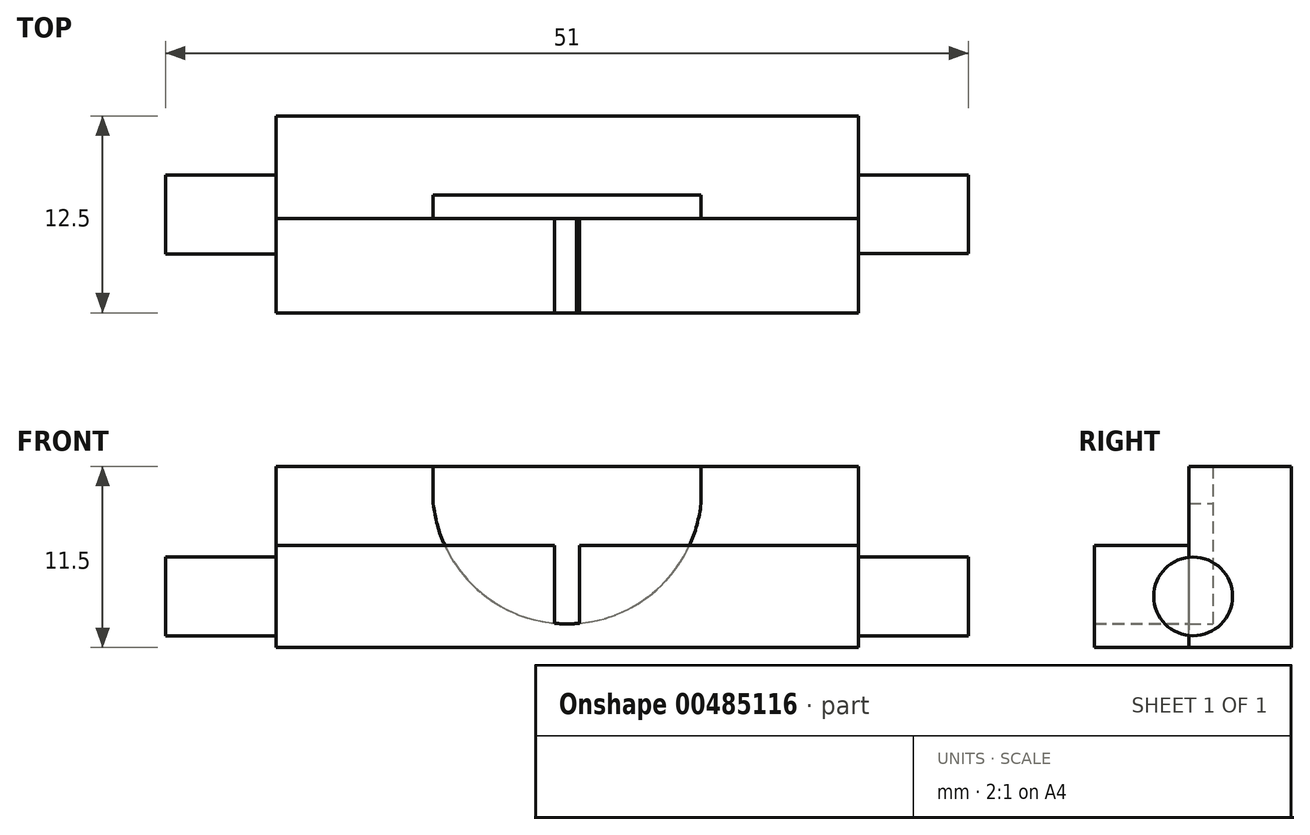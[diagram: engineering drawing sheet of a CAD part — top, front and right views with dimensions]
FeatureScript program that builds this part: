
annotation { "Feature Type Name" : "Feature", "Feature Type Description" : "" }
export const myFeature = defineFeature(function(context is Context, id is Id, definition is map)
    precondition{}
    {
        {
            var Q0;
            Q0=qCreatedBy(makeId("Front.planeOp"),FACE);
            var sketch = newSketch(context, id + "F0", { "sketchPlane" : qUnion([Q0])});
            skLineSegment(sketch, "E0.bottom", {"start": v(-8.5, 7.64) * mm, "end": v(8.5, 7.64) * mm, "construction": true});
            skLineSegment(sketch, "E0.top", {"start": v(-8.5, -7.64) * mm, "end": v(8.5, -7.64) * mm, "construction": true});
            skLineSegment(sketch, "E0.left", {"start": v(-8.5, 7.64) * mm, "end": v(-8.5, -7.64) * mm, "construction": true});
            skLineSegment(sketch, "E0.right", {"start": v(8.5, 7.64) * mm, "end": v(8.5, -7.64) * mm, "construction": true});
            skPoint(sketch, "E0.middle", {"position": v(0, 0) * mm});
            skLineSegment(sketch, "E1", {"start": v(0, 7.64) * mm, "end": v(0, -7.64) * mm, "construction": true});
            skLineSegment(sketch, "E2", {"start": v(-8.5, 0) * mm, "end": v(8.5, 0) * mm, "construction": true});
            skArc(sketch, "E3", {"start": v(-8.5, 0) * mm, "mid": v(0, -7.64) * mm, "end": v(8.5, 0) * mm});
            skLineSegment(sketch, "E4.bottom", {"start": v(-8.5, 7.64) * mm, "end": v(-20.5, 7.64) * mm, "construction": true});
            skLineSegment(sketch, "E4.top", {"start": v(-8.5, -7.64) * mm, "end": v(-20.5, -7.64) * mm, "construction": true});
            skLineSegment(sketch, "E4.right", {"start": v(-20.5, 7.64) * mm, "end": v(-20.5, -7.64) * mm, "construction": true});
            skLineSegment(sketch, "E5.bottom", {"start": v(8.5, 7.64) * mm, "end": v(20.5, 7.64) * mm, "construction": true});
            skLineSegment(sketch, "E5.top", {"start": v(8.5, -7.64) * mm, "end": v(20.5, -7.64) * mm, "construction": true});
            skLineSegment(sketch, "E5.right", {"start": v(20.5, 7.64) * mm, "end": v(20.5, -7.64) * mm, "construction": true});
            skLineSegment(sketch, "E6", {"start": v(-20.5, 2.36) * mm, "end": v(20.5, 2.36) * mm, "construction": true});
            skLineSegment(sketch, "E7", {"start": v(-18.5, 7.64) * mm, "end": v(-18.5, -7.64) * mm, "construction": true});
            skLineSegment(sketch, "E8", {"start": v(18.5, 7.64) * mm, "end": v(18.5, -7.64) * mm, "construction": true});
            skLineSegment(sketch, "E9.bottom", {"start": v(-20.5, -7.64) * mm, "end": v(20.5, -7.64) * mm, "construction": true});
            skLineSegment(sketch, "E9.top", {"start": v(-20.5, -9.14) * mm, "end": v(20.5, -9.14) * mm, "construction": true});
            skLineSegment(sketch, "E9.left", {"start": v(-20.5, -7.64) * mm, "end": v(-20.5, -9.14) * mm, "construction": true});
            skLineSegment(sketch, "E9.right", {"start": v(20.5, -7.64) * mm, "end": v(20.5, -9.14) * mm, "construction": true});
            skLineSegment(sketch, "E10", {"start": v(-18.5, 2.36) * mm, "end": v(-18.5, -9.14) * mm});
            skLineSegment(sketch, "E11", {"start": v(-18.5, -9.14) * mm, "end": v(18.5, -9.14) * mm});
            skLineSegment(sketch, "E12", {"start": v(18.5, -9.14) * mm, "end": v(18.5, 2.36) * mm});
            skLineSegment(sketch, "E13", {"start": v(18.5, 2.36) * mm, "end": v(8.5, 2.36) * mm});
            skLineSegment(sketch, "E14", {"start": v(8.5, 2.36) * mm, "end": v(8.5, 0) * mm});
            skLineSegment(sketch, "E15", {"start": v(-18.5, 2.36) * mm, "end": v(-8.5, 2.36) * mm});
            skLineSegment(sketch, "E16", {"start": v(-8.5, 2.36) * mm, "end": v(-8.5, 0) * mm});
            skLineSegment(sketch, "E17", {"start": v(-8.5, 2.36) * mm, "end": v(8.5, 2.36) * mm});
            skLineSegment(sketch, "E18", {"start": v(-20.5, 7.64) * mm, "end": v(-20.5, -7.64) * mm});
            skLineSegment(sketch, "E19", {"start": v(-20.5, -7.64) * mm, "end": v(-20.5, -9.14) * mm});
            skLineSegment(sketch, "E20", {"start": v(-18.5, -9.14) * mm, "end": v(-20.5, -9.14) * mm});
            skLineSegment(sketch, "E21", {"start": v(20.5, -9.14) * mm, "end": v(18.5, -9.14) * mm});
            skLineSegment(sketch, "E22", {"start": v(20.5, -9.14) * mm, "end": v(20.5, 2.36) * mm});
            skLineSegment(sketch, "E23", {"start": v(18.5, 2.36) * mm, "end": v(20.5, 2.36) * mm});
            skLineSegment(sketch, "E24", {"start": v(-18.5, 2.36) * mm, "end": v(-20.5, 2.36) * mm});
            skLineSegment(sketch, "E25", {"start": v(-20.5, 2.36) * mm, "end": v(-20.5, -9.14) * mm});
            skSolve(sketch);
        }
        {
            var Q0;
            Q0=makeQuery(id+"F0.imprint","IMPRINT",FACE,{"disambiguationData":[TD([[makeQuery(id+"F0.imprint","IMPRINT",EDGE,{"derivedFrom":sQuery(id+"F0.wireOp",EDGE,"E3")}),1.0]])]});
            extrude(context, id + "F1", {"entities" : qUnion([Q0]), "depth" : 5 * mm});
        }
        {
            var Q0;
            Q0=makeQuery(id+"F0.imprint","IMPRINT",FACE,{"disambiguationData":[TD([[makeQuery(id+"F0.imprint","IMPRINT",EDGE,{"derivedFrom":sQuery(id+"F0.wireOp",EDGE,"E3")}),-1.0]])]});
            extrude(context, id + "F2", {"entities" : qUnion([Q0]), "operationType" : NewBodyOperationType.ADD, "depth" : 6.5 * mm});
        }
        {
            var Q0;
            Q0=makeQuery(id+"F2.opExtrude","CAP_FACE",FACE,{"disambiguationData":[OSD([sQuery(id+"F0.wireOp",EDGE,"E3"),sQuery(id+"F0.wireOp",EDGE,"E10"),sQuery(id+"F0.wireOp",EDGE,"E11"),sQuery(id+"F0.wireOp",EDGE,"E12"),sQuery(id+"F0.wireOp",EDGE,"E13"),sQuery(id+"F0.wireOp",EDGE,"E14"),sQuery(id+"F0.wireOp",EDGE,"E15"),sQuery(id+"F0.wireOp",EDGE,"E16")])],"isStart":false});
            var sketch = newSketch(context, id + "F3", { "sketchPlane" : qUnion([Q0])});
            skLineSegment(sketch, "E26", {"start": v(0, -7.64) * mm, "end": v(0, 0) * mm, "construction": true});
            skLineSegment(sketch, "E27", {"start": v(-18.5, 0) * mm, "end": v(-18.5, -9.14) * mm});
            skLineSegment(sketch, "E28", {"start": v(-18.5, -9.14) * mm, "end": v(18.5, -9.14) * mm});
            skLineSegment(sketch, "E29", {"start": v(18.5, -9.14) * mm, "end": v(18.5, 0) * mm});
            skLineSegment(sketch, "E30", {"start": v(0.8, -7.62) * mm, "end": v(-0.6, -7.62) * mm});
            skLineSegment(sketch, "E31", {"start": v(0, -7.64) * mm, "end": v(0, -2.67) * mm, "construction": true});
            skLineSegment(sketch, "E32.bottom", {"start": v(-0.8, -2.67) * mm, "end": v(0.8, -2.67) * mm, "construction": true});
            skLineSegment(sketch, "E32.top", {"start": v(-0.8, -7.62) * mm, "end": v(0.8, -7.62) * mm, "construction": true});
            skLineSegment(sketch, "E32.left", {"start": v(-0.8, -2.67) * mm, "end": v(-0.8, -7.62) * mm, "construction": true});
            skLineSegment(sketch, "E32.right", {"start": v(0.8, -2.67) * mm, "end": v(0.8, -7.62) * mm, "construction": true});
            skLineSegment(sketch, "E33", {"start": v(-0.8, -2.67) * mm, "end": v(-18.5, -2.67) * mm});
            skLineSegment(sketch, "E34", {"start": v(0.8, -2.67) * mm, "end": v(18.5, -2.67) * mm});
            skLineSegment(sketch, "E35", {"start": v(-0.8, -2.67) * mm, "end": v(-0.8, -7.62) * mm});
            skLineSegment(sketch, "E36", {"start": v(0.8, -7.62) * mm, "end": v(0.8, -2.67) * mm});
            skSolve(sketch);
        }
        {
            var Q0;
            {var subQ16=sQuery(id+"F3.wireOp",EDGE,"E28");Q0=makeQuery(id+"F3.imprint","IMPRINT",FACE,{"disambiguationData":[TD([[makeQuery(id+"F3.imprint","IMPRINT",EDGE,{"derivedFrom":subQ16}),1.0]])]});}
            var Q1;
            {var subQ0=sQuery(id+"F3.wireOp",EDGE,"E35");var subQ1=sQuery(id+"F3.wireOp",EDGE,"E33");var subQ2=makeQuery(id+"F3.imprint","INTERSECT",VERTEX,{"derivedFrom":[subQ1,subQ0]});Q1=makeQuery(id+"F3.imprint","IMPRINT",FACE,{"disambiguationData":[TD([[makeQuery(id+"F3.imprint","IMPRINT",EDGE,{"disambiguationData":[TD([[subQ2,-1.0]])],"derivedFrom":subQ1}),1.0]])]});}
            var Q2;
            {var subQ0=sQuery(id+"F3.wireOp",EDGE,"E36");var subQ1=sQuery(id+"F3.wireOp",EDGE,"E34");var subQ2=makeQuery(id+"F3.imprint","INTERSECT",VERTEX,{"derivedFrom":[subQ1,subQ0]});Q2=makeQuery(id+"F3.imprint","IMPRINT",FACE,{"disambiguationData":[TD([[makeQuery(id+"F3.imprint","IMPRINT",EDGE,{"disambiguationData":[TD([[subQ2,-1.0]])],"derivedFrom":subQ1}),-1.0]])]});}
            extrude(context, id + "F4", {"entities" : qUnion([Q0, Q1, Q2]), "depth" : 6 * mm});
        }
        {
            var Q0;
            Q0=makeQuery(id+"F2.opExtrude","SWEPT_FACE",FACE,{"disambiguationData":[OSD([sQuery(id+"F0.wireOp",EDGE,"E12")])]});
            var sketch = newSketch(context, id + "F5", { "sketchPlane" : qUnion([Q0])});
            skLineSegment(sketch, "E37.bottom", {"start": v(0, -9.14) * mm, "end": v(-12.48, -9.14) * mm, "construction": true});
            skLineSegment(sketch, "E37.top", {"start": v(0, -2.65) * mm, "end": v(-12.48, -2.65) * mm, "construction": true});
            skLineSegment(sketch, "E37.left", {"start": v(0, -9.14) * mm, "end": v(0, -2.65) * mm, "construction": true});
            skLineSegment(sketch, "E37.right", {"start": v(-12.48, -9.14) * mm, "end": v(-12.48, -2.65) * mm, "construction": true});
            skLineSegment(sketch, "E38", {"start": v(-12.48, -5.9) * mm, "end": v(0, -5.9) * mm, "construction": true});
            skLineSegment(sketch, "E39", {"start": v(-6.24, -9.14) * mm, "end": v(-6.24, -2.65) * mm, "construction": true});
            skCircle(sketch, "E40", {"center": v(-6.24, -5.9) * mm, "radius": 2.5 * mm});
            skSolve(sketch);
        }
        {
            var Q0;
            {var subQ0=sQuery(id+"F5.wireOp",EDGE,"E40");var subQ1=makeQuery(id+"F2.opExtrude","CAP_EDGE",EDGE,{"disambiguationData":[OSD([sQuery(id+"F0.wireOp",EDGE,"E12")])],"isStart":false});var subQ2=makeQuery(id+"F5.imprint","INTERSECT",VERTEX,{"disambiguationData":[OD(0.0)],"derivedFrom":[subQ1,subQ0]});Q0=makeQuery(id+"F5.imprint","IMPRINT",FACE,{"disambiguationData":[TD([[makeQuery(id+"F5.imprint","IMPRINT",EDGE,{"disambiguationData":[TD([[subQ2,1.0]])],"derivedFrom":subQ0}),1.0]])]});}
            var Q1;
            {var subQ0=sQuery(id+"F5.wireOp",EDGE,"E40");var subQ1=makeQuery(id+"F2.opExtrude","CAP_EDGE",EDGE,{"disambiguationData":[OSD([sQuery(id+"F0.wireOp",EDGE,"E12")])],"isStart":false});var subQ2=makeQuery(id+"F5.imprint","INTERSECT",VERTEX,{"disambiguationData":[OD(0.0)],"derivedFrom":[subQ1,subQ0]});Q1=makeQuery(id+"F5.imprint","IMPRINT",FACE,{"disambiguationData":[TD([[makeQuery(id+"F5.imprint","IMPRINT",EDGE,{"disambiguationData":[TD([[subQ2,-1.0]])],"derivedFrom":subQ0}),1.0]])]});}
            extrude(context, id + "F6", {"entities" : qUnion([Q0, Q1]), "depth" : 7 * mm});
        }
        {
            var Q0;
            Q0=makeQuery(id+"F4.opExtrude","SWEPT_FACE",FACE,{"disambiguationData":[OSD([sQuery(id+"F3.wireOp",EDGE,"E27")])]});
            var sketch = newSketch(context, id + "F7", { "sketchPlane" : qUnion([Q0])});
            skLineSegment(sketch, "E41.bottom", {"start": v(12.5, -9.14) * mm, "end": v(0, -9.14) * mm, "construction": true});
            skLineSegment(sketch, "E41.top", {"start": v(12.5, -2.67) * mm, "end": v(0, -2.67) * mm, "construction": true});
            skLineSegment(sketch, "E41.left", {"start": v(12.5, -9.14) * mm, "end": v(12.5, -2.67) * mm, "construction": true});
            skLineSegment(sketch, "E41.right", {"start": v(0, -9.14) * mm, "end": v(0, -2.67) * mm, "construction": true});
            skLineSegment(sketch, "E42", {"start": v(0, -5.9) * mm, "end": v(12.5, -5.9) * mm, "construction": true});
            skLineSegment(sketch, "E43", {"start": v(6.25, -9.14) * mm, "end": v(6.25, -2.67) * mm, "construction": true});
            skCircle(sketch, "E44", {"center": v(6.25, -5.9) * mm, "radius": 2.5 * mm});
            skSolve(sketch);
        }
        {
            var Q0;
            {var subQ0=sQuery(id+"F7.wireOp",EDGE,"E44");var subQ1=makeQuery(id+"F4.opExtrude","CAP_EDGE",EDGE,{"disambiguationData":[OSD([sQuery(id+"F3.wireOp",EDGE,"E27")])],"isStart":true});var subQ2=makeQuery(id+"F7.imprint","INTERSECT",VERTEX,{"disambiguationData":[OD(0.0)],"derivedFrom":[subQ1,subQ0]});Q0=makeQuery(id+"F7.imprint","IMPRINT",FACE,{"disambiguationData":[TD([[makeQuery(id+"F7.imprint","IMPRINT",EDGE,{"disambiguationData":[TD([[subQ2,1.0]])],"derivedFrom":subQ0}),1.0]])]});}
            var Q1;
            {var subQ0=sQuery(id+"F7.wireOp",EDGE,"E44");var subQ1=makeQuery(id+"F4.opExtrude","CAP_EDGE",EDGE,{"disambiguationData":[OSD([sQuery(id+"F3.wireOp",EDGE,"E27")])],"isStart":true});var subQ2=makeQuery(id+"F7.imprint","INTERSECT",VERTEX,{"disambiguationData":[OD(0.0)],"derivedFrom":[subQ1,subQ0]});Q1=makeQuery(id+"F7.imprint","IMPRINT",FACE,{"disambiguationData":[TD([[makeQuery(id+"F7.imprint","IMPRINT",EDGE,{"disambiguationData":[TD([[subQ2,-1.0]])],"derivedFrom":subQ0}),1.0]])]});}
            extrude(context, id + "F8", {"entities" : qUnion([Q0, Q1]), "depth" : 7 * mm});
        }
    });
